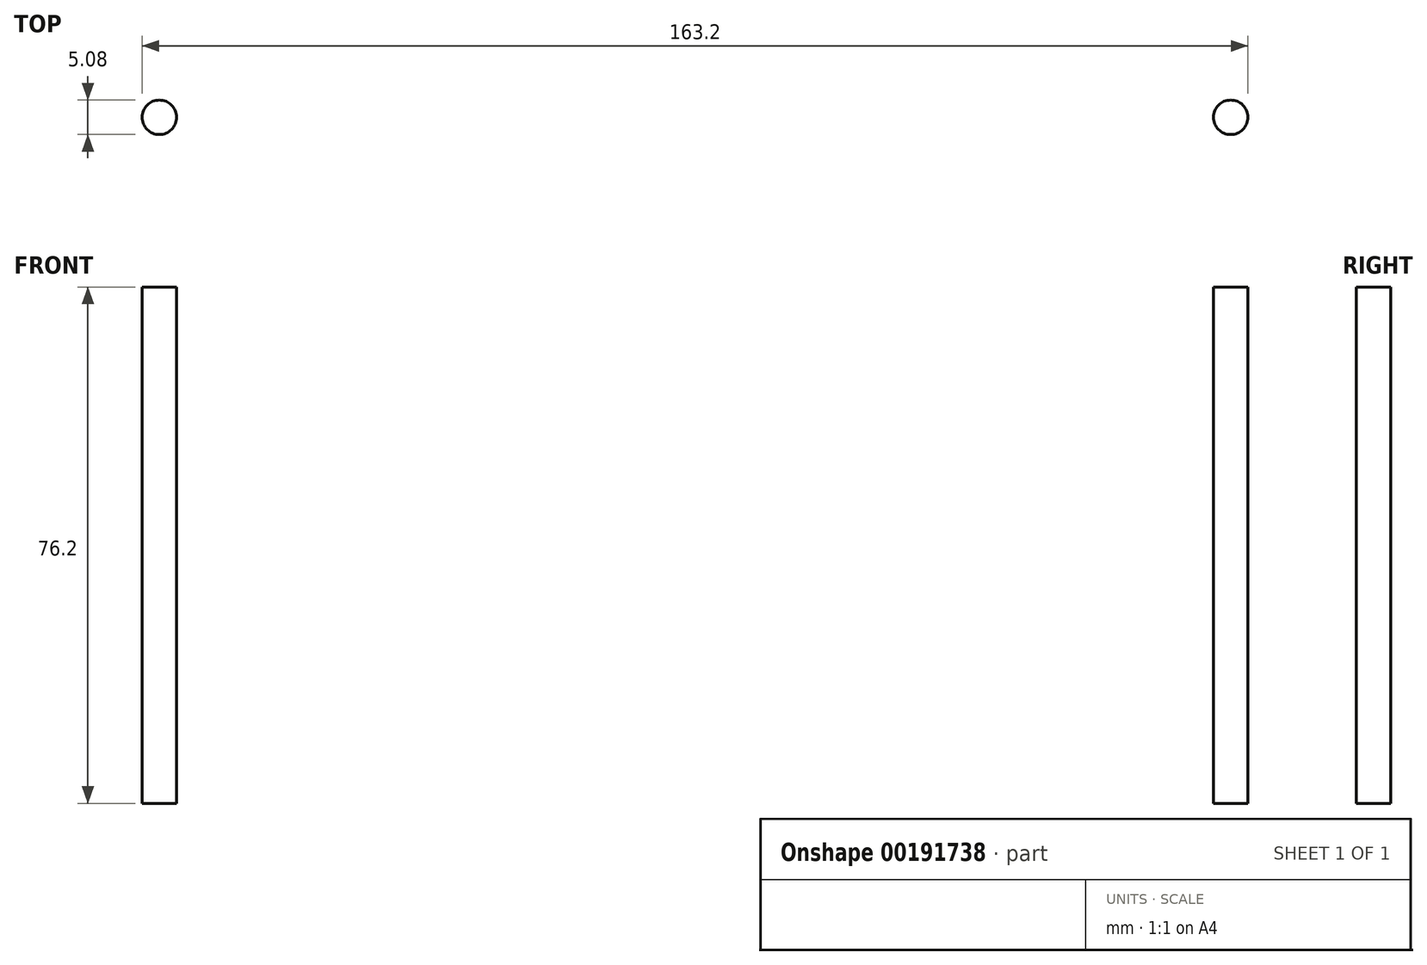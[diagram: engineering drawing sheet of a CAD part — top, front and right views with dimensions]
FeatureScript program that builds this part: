
annotation { "Feature Type Name" : "Feature", "Feature Type Description" : "" }
export const myFeature = defineFeature(function(context is Context, id is Id, definition is map)
    precondition{}
    {
        {
            var Q0;
            Q0=qCreatedBy(makeId("Front.planeOp"),FACE);
            var sketch = newSketch(context, id + "F0", { "sketchPlane" : qUnion([Q0])});
            skLineSegment(sketch, "E0", {"start": v(79.06, 0) * mm, "end": v(79.06, 76.2) * mm});
            skFitSpline(sketch, "E1", {"points": [v(-18.57, 11) * mm, v(-14.74, 204.74) * mm], "startDerivative": vector(3.83, 193.73) * mm, "endDerivative": vector(3.83, 193.73) * mm});
            skFitSpline(sketch, "E2", {"points": [v(38.95, 12.63) * mm, v(41.78, 204.74) * mm], "startDerivative": vector(2.83, 192.1) * mm, "endDerivative": vector(2.83, 192.1) * mm});
            skFitSpline(sketch, "E3", {"points": [v(105.75, 0) * mm, v(106.69, 204.74) * mm], "startDerivative": vector(0.93, 204.74) * mm, "endDerivative": vector(0.93, 204.74) * mm});
            skSolve(sketch);
        }
        {
            var Q0;
            Q0=qCreatedBy(makeId("Top.planeOp"),FACE);
            var sketch = newSketch(context, id + "F1", { "sketchPlane" : qUnion([Q0])});
            skCircle(sketch, "E4", {"center": v(79.06, 0) * mm, "radius": 2.54 * mm});
            skSolve(sketch);
        }
        {
            var Q0;
            Q0=makeQuery(id+"F1.imprint","IMPRINT",FACE,{"disambiguationData":[TD([[makeQuery(id+"F1.imprint","IMPRINT",EDGE,{"derivedFrom":sQuery(id+"F1.wireOp",EDGE,"E4")}),1.0]])]});
            var Q1;
            Q1=sQuery(id+"F0.wireOp",EDGE,"E0");
            sweep(context, id + "F2", {"profiles" : qUnion([Q0]), "path" : qUnion([Q1])});
        }
        {
            var Q0;
            Q0=makeQuery(id+"F2.opSweep","SWEPT_BODY",BODY,{"disambiguationData":[OSD([sQuery(id+"F0.wireOp",EDGE,"E0"),sQuery(id+"F1.wireOp",EDGE,"E4")])]});
            var Q1;
            Q1=qCreatedBy(makeId("Right.planeOp"),FACE);
            mirror(context, id + "F3", {"entities" : qUnion([Q0]), "mirrorPlane" : qUnion([Q1])});
        }
    });
